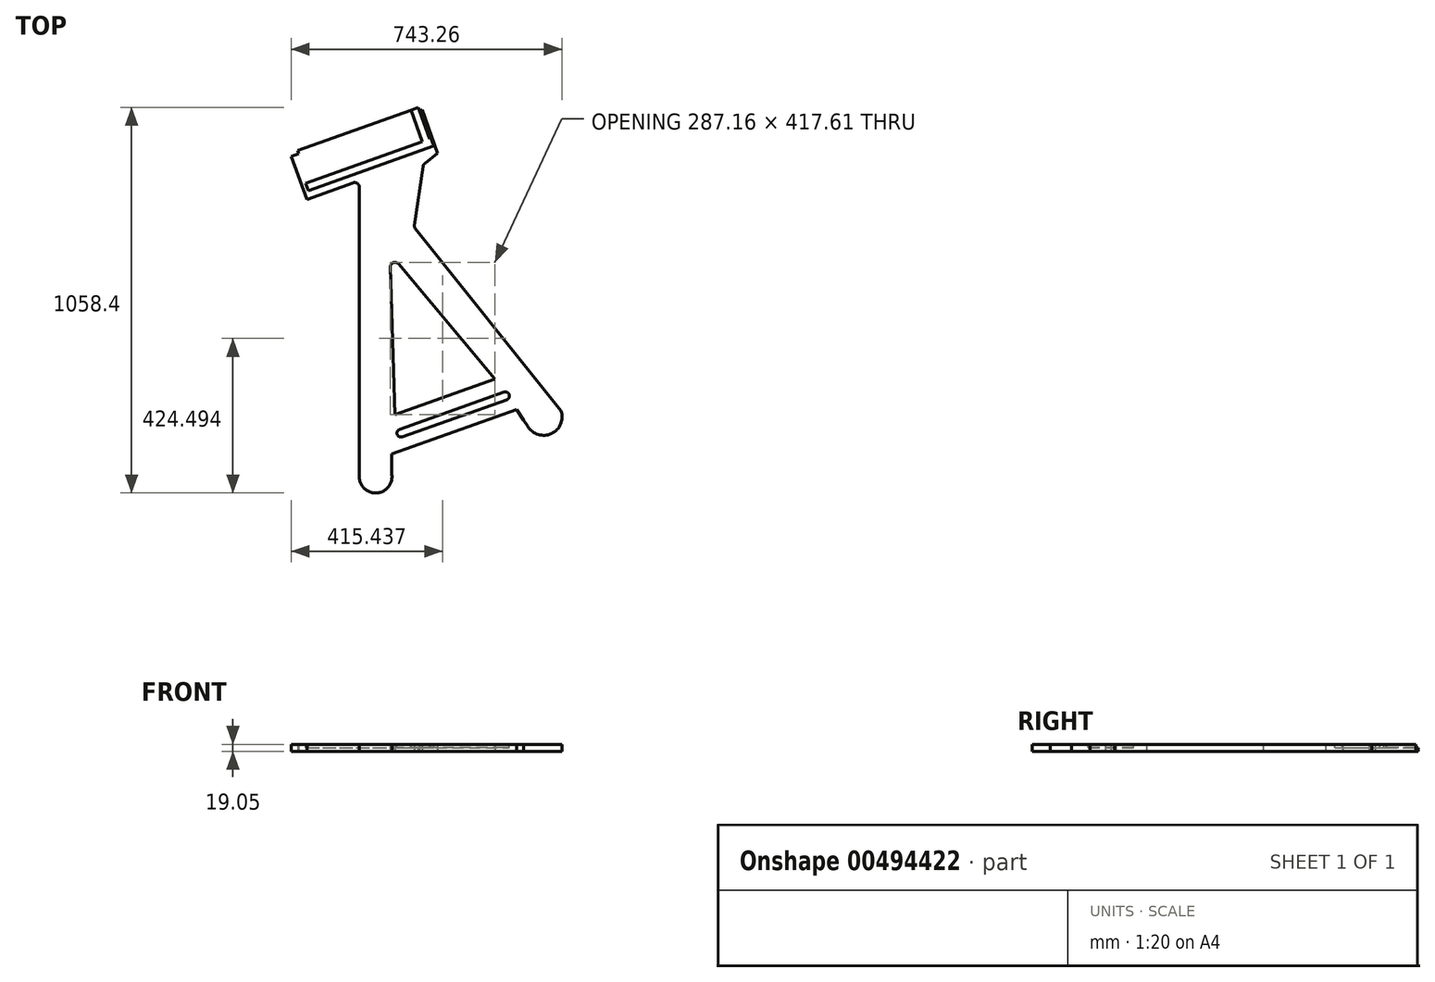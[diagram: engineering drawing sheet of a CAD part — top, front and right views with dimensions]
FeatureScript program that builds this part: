
annotation { "Feature Type Name" : "Feature", "Feature Type Description" : "" }
export const myFeature = defineFeature(function(context is Context, id is Id, definition is map)
    precondition{}
    {
        {
            var Q0;
            Q0=qCreatedBy(makeId("Top.planeOp"),FACE);
            var sketch = newSketch(context, id + "F0", { "sketchPlane" : qUnion([Q0])});
            skLineSegment(sketch, "E0", {"start": v(-306.62, -10.3) * mm, "end": v(-306.88, -10.27) * mm});
            skLineSegment(sketch, "E1", {"start": v(727.27, -283.58) * mm, "end": v(727.27, 427.9) * mm});
            skPoint(sketch, "E2.visualSharp", {"position": v(727.27, -334.1) * mm});
            skPoint(sketch, "E3.visualSharp", {"position": v(828.87, -334.66) * mm});
            skLineSegment(sketch, "E4", {"start": v(902.24, 568.5) * mm, "end": v(878.6, 406.65) * mm});
            skLineSegment(sketch, "E5", {"start": v(727.27, 427.9) * mm, "end": v(727.27, 511.3) * mm});
            skLineSegment(sketch, "E6", {"start": v(710.18, 523.22) * mm, "end": v(584.25, 476.85) * mm});
            skLineSegment(sketch, "E7", {"start": v(584.25, 476.85) * mm, "end": v(540.37, 596.03) * mm});
            skLineSegment(sketch, "E8", {"start": v(540.37, 596.03) * mm, "end": v(561.03, 603.39) * mm});
            skLineSegment(sketch, "E9", {"start": v(899.3, 723.83) * mm, "end": v(941.9, 604.19) * mm});
            skLineSegment(sketch, "E10", {"start": v(906.95, 576.64) * mm, "end": v(941.9, 604.19) * mm});
            skLineSegment(sketch, "E11", {"start": v(540.37, 596.03) * mm, "end": v(561.03, 603.39) * mm, "construction": true});
            skPoint(sketch, "E12.visualSharp", {"position": v(1175.92, -180.14) * mm});
            skLineSegment(sketch, "E13", {"start": v(825.36, -112.6) * mm, "end": v(812.23, 291.9) * mm});
            skLineSegment(sketch, "E14", {"start": v(834.65, 300.48) * mm, "end": v(1099.39, -15.04) * mm});
            skPoint(sketch, "E15.visualSharp", {"position": v(811.04, 328.62) * mm});
            skArc(sketch, "E15.filletArc", {"start": v(834.65, 300.48) * mm, "mid": v(820.38, 304.18) * mm, "end": v(812.23, 291.9) * mm});
            skLineSegment(sketch, "E16", {"start": v(584.25, 476.85) * mm, "end": v(941.9, 604.19) * mm, "construction": true});
            skLineSegment(sketch, "E17", {"start": v(573.92, 504.92) * mm, "end": v(591.86, 511.31) * mm, "construction": true});
            skLineSegment(sketch, "E18", {"start": v(881.25, 396.88) * mm, "end": v(1280.84, -102.55) * mm});
            skLineSegment(sketch, "E19", {"start": v(1185.54, -137.77) * mm, "end": v(1280.84, -102.55) * mm, "construction": true});
            skArc(sketch, "E20", {"start": v(1189.3, -145.4) * mm, "mid": v(1254.36, -165.18) * mm, "end": v(1280.84, -102.55) * mm});
            skLineSegment(sketch, "E21", {"start": v(816.46, -278.8) * mm, "end": v(816.46, -221.1) * mm});
            skLineSegment(sketch, "E22", {"start": v(923.23, 732.35) * mm, "end": v(1268.85, -238.36) * mm, "construction": true});
            skPoint(sketch, "E23.visualSharp", {"position": v(1185.54, -137.77) * mm});
            skPoint(sketch, "E24.visualSharp", {"position": v(877.8, 401.2) * mm});
            skArc(sketch, "E24.filletArc", {"start": v(878.6, 406.65) * mm, "mid": v(878.9, 401.5) * mm, "end": v(881.25, 396.88) * mm});
            skPoint(sketch, "E25.visualSharp", {"position": v(902.97, 573.5) * mm});
            skArc(sketch, "E25.filletArc", {"start": v(906.95, 576.64) * mm, "mid": v(903.81, 573.02) * mm, "end": v(902.24, 568.5) * mm});
            skArc(sketch, "E26.filletArc", {"start": v(727.27, 511.3) * mm, "mid": v(721.83, 521.72) * mm, "end": v(710.18, 523.22) * mm});
            skLineSegment(sketch, "E27", {"start": v(557.84, 612.36) * mm, "end": v(888.53, 730.1) * mm});
            skLineSegment(sketch, "E28", {"start": v(557.84, 612.36) * mm, "end": v(561.03, 603.39) * mm});
            skLineSegment(sketch, "E29", {"start": v(888.53, 730.1) * mm, "end": v(891.73, 721.13) * mm});
            skLineSegment(sketch, "E30.trimOffspring", {"start": v(891.73, 721.13) * mm, "end": v(899.3, 723.83) * mm, "construction": true});
            skLineSegment(sketch, "E31.trimOffspring", {"start": v(891.73, 721.13) * mm, "end": v(899.3, 723.83) * mm});
            skLineSegment(sketch, "E32", {"start": v(1189.3, -145.4) * mm, "end": v(1178.65, -128.04) * mm});
            skLineSegment(sketch, "E33", {"start": v(540.37, 596.03) * mm, "end": v(914.16, -419.2) * mm, "construction": true});
            skLineSegment(sketch, "E34", {"start": v(878.4, -322.07) * mm, "end": v(1232.82, -195.88) * mm, "construction": true});
            skLineSegment(sketch, "E35", {"start": v(816.46, -221.1) * mm, "end": v(1159.46, -98.97) * mm});
            skLineSegment(sketch, "E36", {"start": v(1178.65, -128.04) * mm, "end": v(1159.46, -98.97) * mm});
            skLineSegment(sketch, "E37", {"start": v(825.36, -112.6) * mm, "end": v(1099.39, -15.04) * mm});
            skArc(sketch, "E38", {"start": v(727.27, -283.58) * mm, "mid": v(774.38, -328.23) * mm, "end": v(816.46, -278.8) * mm});
            skSolve(sketch);
        }
        {
            var Q0;
            Q0=makeQuery(id+"F0.imprint","IMPRINT",FACE,{"disambiguationData":[TD([[makeQuery(id+"F0.imprint","IMPRINT",EDGE,{"derivedFrom":sQuery(id+"F0.wireOp",EDGE,"oAVC5DI8-kh1G-Qbfy-uwvq-Txyh6lFHP0Ui")}),1.0]])]});
            var Q1;
            Q1=makeQuery(id+"F0.imprint","IMPRINT",FACE,{"disambiguationData":[TD([[makeQuery(id+"F0.imprint","IMPRINT",EDGE,{"derivedFrom":sQuery(id+"F0.wireOp",EDGE,"E1")}),-1.0]])]});
            extrude(context, id + "F1", {"entities" : qUnion([Q0, Q1]), "depth" : 19.05 * mm});
        }
        {
            var Q0;
            Q0=makeQuery(id+"F1.opExtrude","CAP_FACE",FACE,{"disambiguationData":[OSD([sQuery(id+"F0.wireOp",EDGE,"E1"),sQuery(id+"F0.wireOp",EDGE,"E4"),sQuery(id+"F0.wireOp",EDGE,"E5"),sQuery(id+"F0.wireOp",EDGE,"E6"),sQuery(id+"F0.wireOp",EDGE,"E7"),sQuery(id+"F0.wireOp",EDGE,"E8"),sQuery(id+"F0.wireOp",EDGE,"E9"),sQuery(id+"F0.wireOp",EDGE,"E10"),sQuery(id+"F0.wireOp",EDGE,"E13"),sQuery(id+"F0.wireOp",EDGE,"E14"),sQuery(id+"F0.wireOp",EDGE,"E15.filletArc"),sQuery(id+"F0.wireOp",EDGE,"E18"),sQuery(id+"F0.wireOp",EDGE,"E20"),sQuery(id+"F0.wireOp",EDGE,"E21"),sQuery(id+"F0.wireOp",EDGE,"E24.filletArc"),sQuery(id+"F0.wireOp",EDGE,"E25.filletArc"),sQuery(id+"F0.wireOp",EDGE,"E26.filletArc"),sQuery(id+"F0.wireOp",EDGE,"E27"),sQuery(id+"F0.wireOp",EDGE,"E28"),sQuery(id+"F0.wireOp",EDGE,"E29"),sQuery(id+"F0.wireOp",EDGE,"E31.trimOffspring"),sQuery(id+"F0.wireOp",EDGE,"E32"),sQuery(id+"F0.wireOp",EDGE,"E35"),sQuery(id+"F0.wireOp",EDGE,"E36"),sQuery(id+"F0.wireOp",EDGE,"E37"),sQuery(id+"F0.wireOp",EDGE,"E38")])],"isStart":false});
            var sketch = newSketch(context, id + "F2", { "sketchPlane" : qUnion([Q0])});
            skLineSegment(sketch, "E39", {"start": v(844.81, -174.07) * mm, "end": v(1131.95, -71.83) * mm});
            skLineSegment(sketch, "E40", {"start": v(1124.71, -51.5) * mm, "end": v(837.57, -153.73) * mm});
            skArc(sketch, "E41", {"start": v(1131.95, -71.83) * mm, "mid": v(1138.5, -58.04) * mm, "end": v(1124.71, -51.5) * mm});
            skArc(sketch, "E42", {"start": v(837.57, -153.73) * mm, "mid": v(831.02, -167.52) * mm, "end": v(844.81, -174.07) * mm});
            skSolve(sketch);
        }
        {
            var Q0;
            Q0=qSketchRegion(id+"F2",true);
            extrude(context, id + "F3", {"entities" : qUnion([Q0]), "operationType" : NewBodyOperationType.REMOVE, "oppositeDirection" : true, "depth" : 9.52 * mm});
        }
        {
            var Q0;
            Q0=makeQuery(id+"F1.opExtrude","CAP_FACE",FACE,{"disambiguationData":[OSD([sQuery(id+"F0.wireOp",EDGE,"E1"),sQuery(id+"F0.wireOp",EDGE,"E4"),sQuery(id+"F0.wireOp",EDGE,"E5"),sQuery(id+"F0.wireOp",EDGE,"E6"),sQuery(id+"F0.wireOp",EDGE,"E7"),sQuery(id+"F0.wireOp",EDGE,"E8"),sQuery(id+"F0.wireOp",EDGE,"E9"),sQuery(id+"F0.wireOp",EDGE,"E10"),sQuery(id+"F0.wireOp",EDGE,"E13"),sQuery(id+"F0.wireOp",EDGE,"E14"),sQuery(id+"F0.wireOp",EDGE,"E15.filletArc"),sQuery(id+"F0.wireOp",EDGE,"E18"),sQuery(id+"F0.wireOp",EDGE,"E20"),sQuery(id+"F0.wireOp",EDGE,"E21"),sQuery(id+"F0.wireOp",EDGE,"E24.filletArc"),sQuery(id+"F0.wireOp",EDGE,"E25.filletArc"),sQuery(id+"F0.wireOp",EDGE,"E26.filletArc"),sQuery(id+"F0.wireOp",EDGE,"E27"),sQuery(id+"F0.wireOp",EDGE,"E28"),sQuery(id+"F0.wireOp",EDGE,"E29"),sQuery(id+"F0.wireOp",EDGE,"E31.trimOffspring"),sQuery(id+"F0.wireOp",EDGE,"E32"),sQuery(id+"F0.wireOp",EDGE,"E35"),sQuery(id+"F0.wireOp",EDGE,"E36"),sQuery(id+"F0.wireOp",EDGE,"E37"),sQuery(id+"F0.wireOp",EDGE,"E38")])],"isStart":false});
            var sketch = newSketch(context, id + "F4", { "sketchPlane" : qUnion([Q0])});
            skLineSegment(sketch, "E43.bottom", {"start": v(587.55, 502.16) * mm, "end": v(931.59, 624.65) * mm});
            skLineSegment(sketch, "E43.top", {"start": v(580.31, 522.5) * mm, "end": v(899.8, 636.25) * mm});
            skLineSegment(sketch, "E43.left", {"start": v(587.55, 502.16) * mm, "end": v(580.31, 522.5) * mm});
            skLineSegment(sketch, "E44", {"start": v(868.5, 724.16) * mm, "end": v(899.8, 636.25) * mm});
            skPoint(sketch, "E45.0", {"position": v(892.1, 722.26) * mm});
            skPoint(sketch, "E46.0", {"position": v(888.9, 731.23) * mm});
            skLineSegment(sketch, "E47", {"start": v(888.9, 731.23) * mm, "end": v(892.1, 722.26) * mm});
            skLineSegment(sketch, "E48", {"start": v(888.9, 731.23) * mm, "end": v(868.5, 724.16) * mm});
            skLineSegment(sketch, "E49", {"start": v(920.2, 643.31) * mm, "end": v(892.1, 722.26) * mm});
            skLineSegment(sketch, "E50", {"start": v(920.2, 643.31) * mm, "end": v(924.4, 644.81) * mm});
            skLineSegment(sketch, "E51", {"start": v(931.59, 624.65) * mm, "end": v(924.4, 644.81) * mm});
            skSolve(sketch);
        }
        {
            var Q0;
            Q0=qSketchRegion(id+"F4",true);
            extrude(context, id + "F5", {"entities" : qUnion([Q0]), "operationType" : NewBodyOperationType.REMOVE, "oppositeDirection" : true, "depth" : 9.52 * mm});
        }
    });
